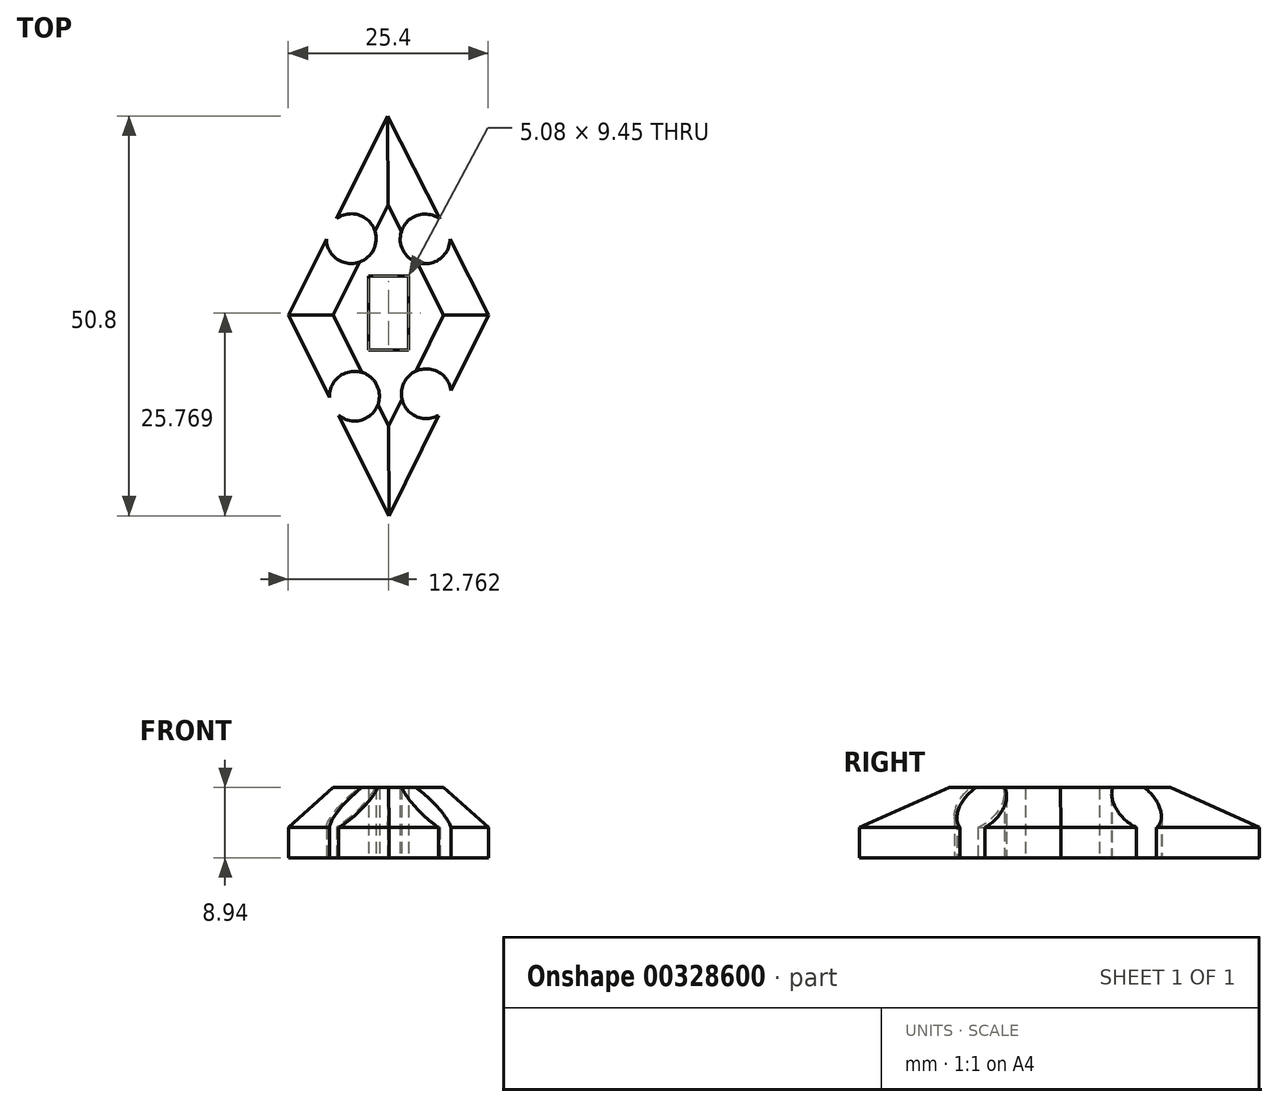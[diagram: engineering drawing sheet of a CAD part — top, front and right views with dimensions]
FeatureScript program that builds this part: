
annotation { "Feature Type Name" : "Feature", "Feature Type Description" : "" }
export const myFeature = defineFeature(function(context is Context, id is Id, definition is map)
    precondition{}
    {
        {
            var Q0;
            Q0=qCreatedBy(makeId("Top.planeOp"),FACE);
            var sketch = newSketch(context, id + "F0", { "sketchPlane" : qUnion([Q0])});
            skLineSegment(sketch, "E0", {"start": v(0.63, 31.55) * mm, "end": v(-5.89, 18.51) * mm});
            skLineSegment(sketch, "E1", {"start": v(-12, 6.3) * mm, "end": v(-6.75, -4.19) * mm});
            skLineSegment(sketch, "E2", {"start": v(0.78, -19.25) * mm, "end": v(7.1, -6.47) * mm});
            skLineSegment(sketch, "E3", {"start": v(13.4, 6.3) * mm, "end": v(8.54, 15.92) * mm});
            skArc(sketch, "E4", {"start": v(7.24, 18.49) * mm, "mid": v(2.55, 14.5) * mm, "end": v(8.54, 15.92) * mm});
            skArc(sketch, "E5.MirrorCS", {"start": v(-5.89, 18.51) * mm, "mid": v(-1.18, 14.56) * mm, "end": v(-7.17, 15.95) * mm});
            skArc(sketch, "E6.MirrorCS", {"start": v(7.1, -6.47) * mm, "mid": v(2.7, -2.32) * mm, "end": v(8.66, -3.3) * mm});
            skArc(sketch, "E7.MirrorCS", {"start": v(-5.6, -6.47) * mm, "mid": v(-0.77, -2.62) * mm, "end": v(-6.75, -4.19) * mm});
            skLineSegment(sketch, "E8.trimOffspring", {"start": v(8.66, -3.3) * mm, "end": v(13.4, 6.3) * mm});
            skLineSegment(sketch, "E9.trimOffspring", {"start": v(7.24, 18.49) * mm, "end": v(0.63, 31.55) * mm});
            skLineSegment(sketch, "E10.trimOffspring", {"start": v(-7.17, 15.95) * mm, "end": v(-12, 6.3) * mm});
            skLineSegment(sketch, "E11.trimOffspring", {"start": v(-5.6, -6.47) * mm, "end": v(0.78, -19.25) * mm});
            skLineSegment(sketch, "E12.bottom", {"start": v(-1.78, 11.24) * mm, "end": v(3.3, 11.24) * mm});
            skLineSegment(sketch, "E12.top", {"start": v(-1.78, 1.8) * mm, "end": v(3.3, 1.8) * mm});
            skLineSegment(sketch, "E12.left", {"start": v(-1.78, 11.24) * mm, "end": v(-1.78, 1.8) * mm});
            skLineSegment(sketch, "E12.right", {"start": v(3.3, 11.24) * mm, "end": v(3.3, 1.8) * mm});
            skSolve(sketch);
        }
        {
            var Q0;
            Q0 = qSketchRegion(id + "F0", true);
            extrude(context, id + "F1", {"entities" : qUnion([Q0]), "depth" : 8.94 * mm});
        }
        {
            var Q0;
            Q0=makeQuery(id+"F1.opExtrude","CAP_EDGE",EDGE,{"disambiguationData":[OSD([sQuery(id+"F0.wireOp",EDGE,"E9.trimOffspring")])],"isStart":false});
            var Q1;
            Q1=makeQuery(id+"F1.opExtrude","CAP_EDGE",EDGE,{"disambiguationData":[OSD([sQuery(id+"F0.wireOp",EDGE,"E0")])],"isStart":false});
            var Q2;
            Q2=makeQuery(id+"F1.opExtrude","CAP_EDGE",EDGE,{"disambiguationData":[OSD([sQuery(id+"F0.wireOp",EDGE,"E10.trimOffspring")])],"isStart":false});
            var Q3;
            Q3=makeQuery(id+"F1.opExtrude","CAP_EDGE",EDGE,{"disambiguationData":[OSD([sQuery(id+"F0.wireOp",EDGE,"E1")])],"isStart":false});
            var Q4;
            Q4=makeQuery(id+"F1.opExtrude","CAP_EDGE",EDGE,{"disambiguationData":[OSD([sQuery(id+"F0.wireOp",EDGE,"E11.trimOffspring")])],"isStart":false});
            var Q5;
            Q5=makeQuery(id+"F1.opExtrude","CAP_EDGE",EDGE,{"disambiguationData":[OSD([sQuery(id+"F0.wireOp",EDGE,"E2")])],"isStart":false});
            var Q6;
            Q6=makeQuery(id+"F1.opExtrude","CAP_EDGE",EDGE,{"disambiguationData":[OSD([sQuery(id+"F0.wireOp",EDGE,"E8.trimOffspring")])],"isStart":false});
            var Q7;
            Q7=makeQuery(id+"F1.opExtrude","CAP_EDGE",EDGE,{"disambiguationData":[OSD([sQuery(id+"F0.wireOp",EDGE,"E3")])],"isStart":false});
            chamfer(context, id + "F2", {"entities" : qUnion([Q0, Q1, Q2, Q3, Q4, Q5, Q6, Q7]), "width" : 5.08 * mm, "tangentPropagation" : true});
        }
    });
